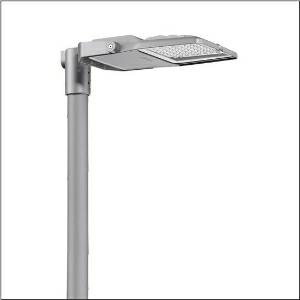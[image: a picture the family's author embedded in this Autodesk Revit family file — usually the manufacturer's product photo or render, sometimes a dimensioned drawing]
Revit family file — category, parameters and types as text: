
# Revit family: floodlight_fl_21_iq_mini___pl52_5xa7771c2d3a_33da
name_source: partatom
category: Lighting Fixtures
units: mm (PartAtom-declared; Revit-internal decimal feet)

## family parameters
Cut with Voids When Loaded = No
Host = Face
Light Source = No
Part Type = Normal
Room Calculation Point = No
Round Connector Dimension = Use Diameter
Shared = No

## types (1)
- --- (1 x LED, 12210 lm, 87.2 W, 3000K)
    Apparent Load = 87 VA
    CIE Flux Codes = 26 60 98 100 100
    Color Rendering = 70
    Color Temperature = 3000K
    Default Elevation = 1800 mm
    Description = Floodlight FL 21 iQ mini, floodlight, primary light control with lens, of PMMA, primary optical cover: protective disc, of toughened safety glass, transparent, light distribution: PL52, light emission: direct distribution, installation type: surface-mounted, LED, High Power LED, rated luminous flux: 12.210lm, luminous efficacy: 140lm/W, light colour: 730, colour temperature: 3000K, control gear: iQ Comfort/DALI, control: Auto-Match, Temp-Guard, Lumen-Switch, Night-Set, Smart-Wire, Light-Fading, Desk-Remote (wireless, voltage-free reading and setting of iQ features in the workshop via application-optimized NFC function/RFID function), optimised constant luminous flux control (CLO 2.0), with terminal, 6-pole, mains connection: 220..240V, AC, 50/60Hz, start of lifetime: 87W, end of service life: 92W, reduction: 40W, luminaire housing, of diecast aluminium, powder-coated, Siteco® metallic grey (DB 702S), corrosivity category C5 mid according to DIN EN ISO 12944, suitable for swimming pools, chlorine-resistant, sealing non-destructively replaceable, please order mast flange separately, mast bracket, of steel, galvanised, powder-coated, Siteco® metallic grey (DB 702S), protection rating (complete): IP66, insulation class (complete): insulation class II (safety insulation), certification: CE, ENEC, VDE, protection symbol: D, impact resistance: IK08, permissible operating ambient temperature: -40..+40°C, permissible operating ambient temperature for outdoor applications: -40..+50°C, standard: DIN EN 12944, LABS conformity tested according to VDMA 24364:2018-05, packaging unit: 1 piece

Light Distribution: PL52
    Height = 70 mm
    Lamp = 1 x LED
    Lamp Light Flux = 12210 lm
    Lamp Power = 87.2 W
    Lamp count = 1
    Length = 485 mm
    Luminous efficacy = 140 lm/W
    Manufacturer = Siteco
    ModVariant = No
    Model = 5XA7771C2D3A
    Number of Poles = 1
    OnlyDefault = Yes
    Power Factor = 1
    Product Name = Floodlight FL 21 iQ mini | PL52
    Product group = floodlight | pylon annexe
    ProductGroupID = 6200
    Protection Class = Protection class II
    Protection Degree = IP 66
    RLX_Detail_Level = 1
    RLX_Emergency_Light_Flux = 0 lm
    RLX_Emergency_Type = 0
    RLX_Emergency_Type_DB = No
    RlxData = <blob elided: 101493 chars, md5=6feeb3d8>
    Socket = socket
    Standby Power = 0 W
    System Light Flux = 12210 lm
    System Power = 87 W
    Type Comments = factory setting: luminous flux: 100 % | dim-lin: 254 | 456 mA
    Type Image = l_1007125.jpg
    URL = http://relux.com
    VarID = @adj_164556
    Voltage = 0 V
    Weight = 0.00 kg
    Width = 337 mm

## geometry (parser evidence)
native form markers: Blend x4, Sweep x11
no freeform markers — native parametric forms only
